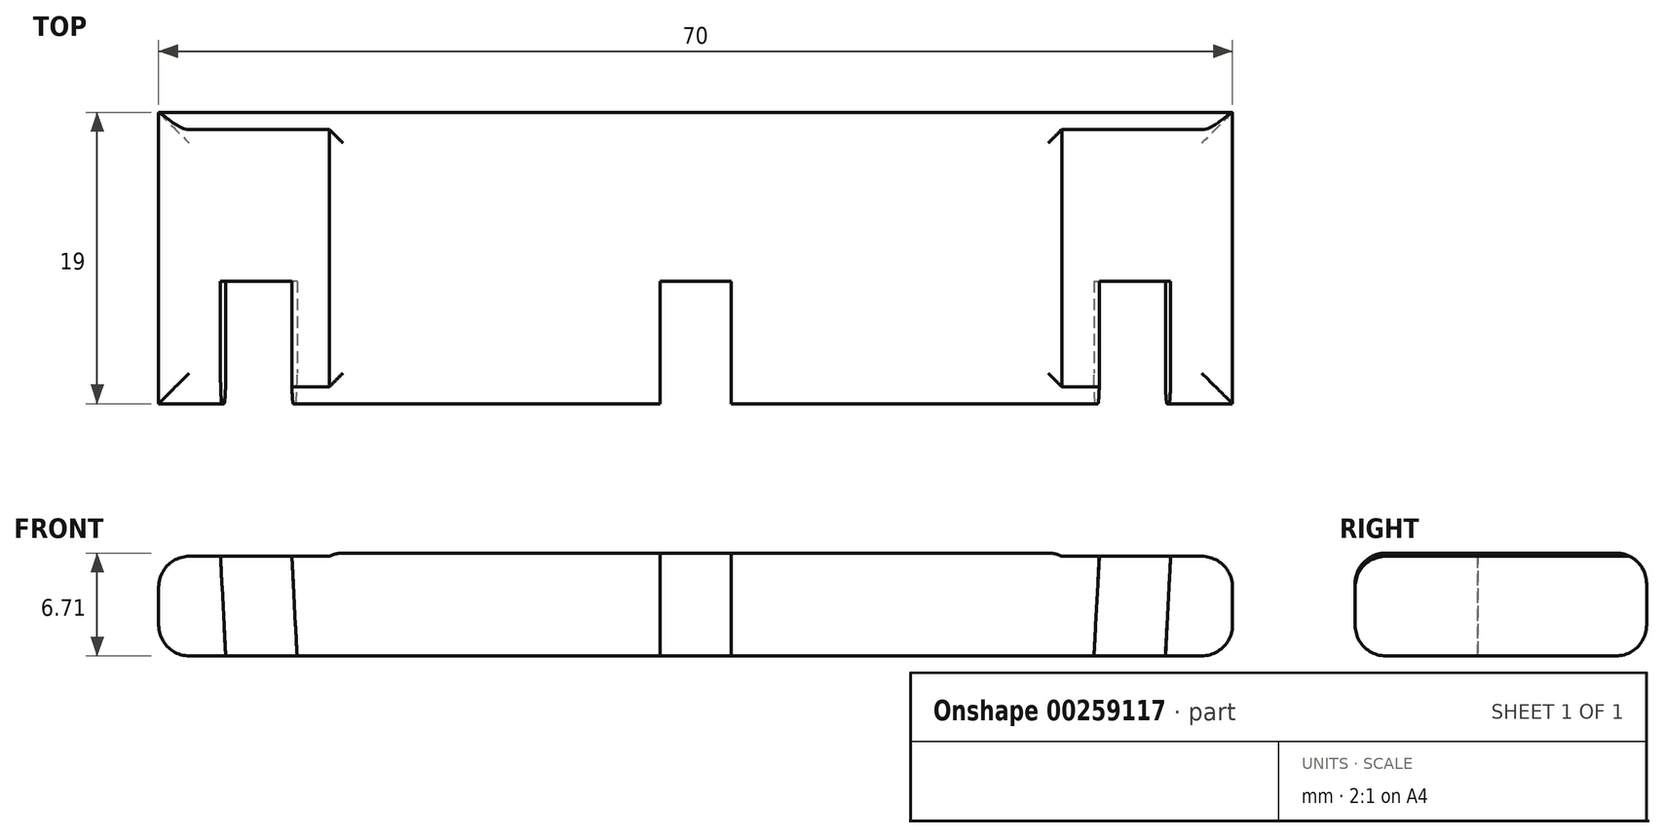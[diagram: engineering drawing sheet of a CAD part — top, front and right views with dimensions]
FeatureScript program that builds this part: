
annotation { "Feature Type Name" : "Feature", "Feature Type Description" : "" }
export const myFeature = defineFeature(function(context is Context, id is Id, definition is map)
    precondition{}
    {
        {
            var Q0;
            Q0=qCreatedBy(makeId("Top.planeOp"),FACE);
            var sketch = newSketch(context, id + "F0", { "sketchPlane" : qUnion([Q0])});
            skLineSegment(sketch, "E0.bottom", {"start": v(35, -9.5) * mm, "end": v(-35, -9.5) * mm});
            skLineSegment(sketch, "E0.top", {"start": v(35, 9.5) * mm, "end": v(-35, 9.5) * mm});
            skLineSegment(sketch, "E0.left", {"start": v(35, -9.5) * mm, "end": v(35, 9.5) * mm});
            skLineSegment(sketch, "E0.right", {"start": v(-35, -9.5) * mm, "end": v(-35, 9.5) * mm});
            skPoint(sketch, "E0.middle", {"position": v(0, 0) * mm});
            skLineSegment(sketch, "E1", {"start": v(0, 0) * mm, "end": v(0, -9.5) * mm, "construction": true});
            skLineSegment(sketch, "E2.bottom", {"start": v(2.33, -17.5) * mm, "end": v(-2.32, -17.5) * mm});
            skLineSegment(sketch, "E2.top", {"start": v(2.33, -1.5) * mm, "end": v(-2.33, -1.5) * mm});
            skLineSegment(sketch, "E2.left", {"start": v(2.33, -17.5) * mm, "end": v(2.33, -1.5) * mm});
            skLineSegment(sketch, "E2.right", {"start": v(-2.32, -17.5) * mm, "end": v(-2.32, -1.5) * mm});
            skPoint(sketch, "E2.middle", {"position": v(0, -9.5) * mm});
            skLineSegment(sketch, "E3.1.0.0", {"start": v(25.98, -17.5) * mm, "end": v(25.98, -1.5) * mm});
            skLineSegment(sketch, "E3.1.0.1", {"start": v(30.63, -1.5) * mm, "end": v(25.98, -1.5) * mm});
            skLineSegment(sketch, "E3.1.0.2", {"start": v(30.63, -17.5) * mm, "end": v(30.63, -1.5) * mm});
            skLineSegment(sketch, "E3.direction1", {"start": v(-2.32, -17.5) * mm, "end": v(25.98, -17.5) * mm, "construction": true});
            skLineSegment(sketch, "E4.1.0.0", {"start": v(-25.98, -1.5) * mm, "end": v(-30.63, -1.5) * mm});
            skLineSegment(sketch, "E4.1.0.1", {"start": v(-30.62, -17.5) * mm, "end": v(-30.62, -1.5) * mm});
            skLineSegment(sketch, "E4.1.0.2", {"start": v(-25.97, -17.5) * mm, "end": v(-25.97, -1.5) * mm});
            skLineSegment(sketch, "E4.direction1", {"start": v(-2.32, -17.5) * mm, "end": v(-30.62, -17.5) * mm, "construction": true});
            skLineSegment(sketch, "E5", {"start": v(-23.87, -9.5) * mm, "end": v(-23.87, 9.5) * mm});
            skLineSegment(sketch, "E6.MirrorCS", {"start": v(23.87, -9.5) * mm, "end": v(23.87, 9.5) * mm});
            skSolve(sketch);
        }
        {
            var Q0;
            {var subQ0=sQuery(id+"F0.wireOp",EDGE,"E2.top");Q0=makeQuery(id+"F0.imprint","IMPRINT",FACE,{"disambiguationData":[TD([[makeQuery(id+"F0.imprint","IMPRINT",EDGE,{"derivedFrom":subQ0}),-1.0]])]});}
            extrude(context, id + "F1", {"entities" : qUnion([Q0]), "depth" : 6.7 * mm});
        }
        {
            var Q0;
            {var subQ0=sQuery(id+"F0.wireOp",EDGE,"E0.right");Q0=makeQuery(id+"F0.imprint","IMPRINT",FACE,{"disambiguationData":[TD([[makeQuery(id+"F0.imprint","IMPRINT",EDGE,{"derivedFrom":subQ0}),-1.0]])]});}
            var Q1;
            {var subQ0=sQuery(id+"F0.wireOp",EDGE,"E0.left");Q1=makeQuery(id+"F0.imprint","IMPRINT",FACE,{"disambiguationData":[TD([[makeQuery(id+"F0.imprint","IMPRINT",EDGE,{"derivedFrom":subQ0}),1.0]])]});}
            var Q2;
            {var subQ5=sQuery(id+"F0.wireOp",EDGE,"E4.1.0.0");Q2=makeQuery(id+"F0.imprint","IMPRINT",FACE,{"disambiguationData":[TD([[makeQuery(id+"F0.imprint","IMPRINT",EDGE,{"derivedFrom":subQ5}),1.0]])]});}
            var Q3;
            {var subQ5=sQuery(id+"F0.wireOp",EDGE,"E3.1.0.1");Q3=makeQuery(id+"F0.imprint","IMPRINT",FACE,{"disambiguationData":[TD([[makeQuery(id+"F0.imprint","IMPRINT",EDGE,{"derivedFrom":subQ5}),1.0]])]});}
            extrude(context, id + "F2", {"entities" : qUnion([Q0, Q1, Q2, Q3]), "operationType" : NewBodyOperationType.ADD, "depth" : 6.5 * mm});
        }
        {
            var Q0;
            {var subQ0=sQuery(id+"F0.wireOp",EDGE,"E0.bottom");var subQ2=makeQuery(id+"F0.imprint","INTERSECT",VERTEX,{"derivedFrom":[subQ0,sQuery(id+"F0.wireOp",EDGE,"E4.1.0.2")]});var subQ3=makeQuery(id+"F0.imprint","INTERSECT",VERTEX,{"derivedFrom":[subQ0,sQuery(id+"F0.wireOp",EDGE,"E5")]});Q0=makeQuery(id+"F2.boolean.opBoolean","MERGE",FACE,{"derivedFrom":[makeQuery(id+"F1.opExtrude","SWEPT_FACE",FACE,{"disambiguationData":[OSD([subQ0]),TDD([makeQuery(id+"F0.imprint","IMPRINT",EDGE,{"disambiguationData":[TD([[subQ3,1.0]])],"derivedFrom":subQ0})])]}),makeQuery(id+"F2.opExtrude","SWEPT_FACE",FACE,{"disambiguationData":[OSD([subQ0]),TDD([makeQuery(id+"F0.imprint","IMPRINT",EDGE,{"disambiguationData":[TD([[subQ3,-1.0]])],"derivedFrom":subQ0}),makeQuery(id+"F0.imprint","IMPRINT",EDGE,{"disambiguationData":[TD([[subQ2,-1.0]])],"derivedFrom":subQ0}),makeQuery(id+"F0.imprint","IMPRINT",EDGE,{"disambiguationData":[TD([[makeQuery(id+"F0.imprint","INTERSECT",VERTEX,{"derivedFrom":[subQ0,sQuery(id+"F0.wireOp",EDGE,"E0.right")]}),1.0]])],"derivedFrom":subQ0})])]})]});}
            var sketch = newSketch(context, id + "F3", { "sketchPlane" : qUnion([Q0])});
            skLineSegment(sketch, "E7", {"start": v(-25.97, 6.7) * mm, "end": v(-25.97, 0) * mm, "construction": true});
            skLineSegment(sketch, "E8", {"start": v(-25.97, 0) * mm, "end": v(-26.32, 6.5) * mm});
            skLineSegment(sketch, "E9.0", {"start": v(-30.63, 0) * mm, "end": v(-30.97, 6.5) * mm});
            skLineSegment(sketch, "E10", {"start": v(25.97, 0) * mm, "end": v(25.97, 6.52) * mm, "construction": true});
            skLineSegment(sketch, "E11", {"start": v(25.97, 0) * mm, "end": v(26.34, 6.97) * mm});
            skLineSegment(sketch, "E12.0", {"start": v(30.62, -0.24) * mm, "end": v(30.98, 6.73) * mm});
            skLineSegment(sketch, "E13", {"start": v(26.34, 6.97) * mm, "end": v(30.98, 6.73) * mm});
            skLineSegment(sketch, "E14", {"start": v(30.62, -0.24) * mm, "end": v(25.97, 0) * mm});
            skSolve(sketch);
        }
        {
            var Q0;
            {var subQ0=sQuery(id+"F3.wireOp",EDGE,"E8");Q0=makeQuery(id+"F3.imprint","IMPRINT",FACE,{"disambiguationData":[TD([[makeQuery(id+"F3.imprint","IMPRINT",EDGE,{"derivedFrom":subQ0}),1.0]])]});}
            var Q1;
            Q1=makeQuery(id+"F3.imprint","IMPRINT",FACE,{"disambiguationData":[TD([[makeQuery(id+"F3.imprint","IMPRINT",EDGE,{"derivedFrom":sQuery(id+"F3.wireOp",EDGE,"E11")}),-1.0]])]});
            extrude(context, id + "F4", {"entities" : qUnion([Q0, Q1]), "operationType" : NewBodyOperationType.REMOVE, "oppositeDirection" : true, "depth" : 8 * mm});
        }
        {
            var Q0;
            Q0=makeQuery(id+"F1.opExtrude","CAP_EDGE",EDGE,{"disambiguationData":[OSD([sQuery(id+"F0.wireOp",EDGE,"E0.top")])],"isStart":false});
            var Q1;
            Q1=makeQuery(id+"F1.opExtrude","CAP_EDGE",EDGE,{"disambiguationData":[OSD([sQuery(id+"F0.wireOp",EDGE,"E0.right")])],"isStart":false});
            var Q2;
            {var subQ0=sQuery(id+"F0.wireOp",EDGE,"E0.bottom");Q2=makeQuery(id+"F1.opExtrude","CAP_EDGE",EDGE,{"disambiguationData":[OSD([subQ0]),TDD([makeQuery(id+"F0.imprint","IMPRINT",EDGE,{"disambiguationData":[TD([[makeQuery(id+"F0.imprint","INTERSECT",VERTEX,{"derivedFrom":[subQ0,sQuery(id+"F0.wireOp",EDGE,"E4.1.0.2")]}),1.0]])],"derivedFrom":subQ0})])],"isStart":false});}
            var Q3;
            {var subQ0=sQuery(id+"F0.wireOp",EDGE,"E0.bottom");Q3=makeQuery(id+"F1.opExtrude","CAP_EDGE",EDGE,{"disambiguationData":[OSD([subQ0]),TDD([makeQuery(id+"F0.imprint","IMPRINT",EDGE,{"disambiguationData":[TD([[makeQuery(id+"F0.imprint","INTERSECT",VERTEX,{"derivedFrom":[subQ0,sQuery(id+"F0.wireOp",EDGE,"E0.right")]}),1.0]])],"derivedFrom":subQ0})])],"isStart":false});}
            var Q4;
            {var subQ0=sQuery(id+"F0.wireOp",EDGE,"E0.bottom");Q4=makeQuery(id+"F1.opExtrude","CAP_EDGE",EDGE,{"disambiguationData":[OSD([subQ0]),TDD([makeQuery(id+"F0.imprint","IMPRINT",EDGE,{"disambiguationData":[TD([[makeQuery(id+"F0.imprint","INTERSECT",VERTEX,{"derivedFrom":[subQ0,sQuery(id+"F0.wireOp",EDGE,"E3.1.0.0")]}),-1.0]])],"derivedFrom":subQ0})])],"isStart":false});}
            var Q5;
            {var subQ0=sQuery(id+"F0.wireOp",EDGE,"E0.bottom");Q5=makeQuery(id+"F1.opExtrude","CAP_EDGE",EDGE,{"disambiguationData":[OSD([subQ0]),TDD([makeQuery(id+"F0.imprint","IMPRINT",EDGE,{"disambiguationData":[TD([[makeQuery(id+"F0.imprint","INTERSECT",VERTEX,{"derivedFrom":[subQ0,sQuery(id+"F0.wireOp",EDGE,"E0.left")]}),-1.0]])],"derivedFrom":subQ0})])],"isStart":false});}
            var Q6;
            {var subQ0=sQuery(id+"F0.wireOp",EDGE,"E0.bottom");Q6=makeQuery(id+"F1.opExtrude","CAP_EDGE",EDGE,{"disambiguationData":[OSD([subQ0]),TDD([makeQuery(id+"F0.imprint","IMPRINT",EDGE,{"disambiguationData":[TD([[makeQuery(id+"F0.imprint","INTERSECT",VERTEX,{"derivedFrom":[subQ0,sQuery(id+"F0.wireOp",EDGE,"E3.1.0.0")]}),-1.0]])],"derivedFrom":subQ0})])],"isStart":true});}
            var Q7;
            {var subQ0=sQuery(id+"F0.wireOp",EDGE,"E0.bottom");Q7=makeQuery(id+"F1.opExtrude","CAP_EDGE",EDGE,{"disambiguationData":[OSD([subQ0]),TDD([makeQuery(id+"F0.imprint","IMPRINT",EDGE,{"disambiguationData":[TD([[makeQuery(id+"F0.imprint","INTERSECT",VERTEX,{"derivedFrom":[subQ0,sQuery(id+"F0.wireOp",EDGE,"E4.1.0.2")]}),1.0]])],"derivedFrom":subQ0})])],"isStart":true});}
            var Q8;
            {var subQ0=sQuery(id+"F0.wireOp",EDGE,"E0.bottom");Q8=makeQuery(id+"F1.opExtrude","CAP_EDGE",EDGE,{"disambiguationData":[OSD([subQ0]),TDD([makeQuery(id+"F0.imprint","IMPRINT",EDGE,{"disambiguationData":[TD([[makeQuery(id+"F0.imprint","INTERSECT",VERTEX,{"derivedFrom":[subQ0,sQuery(id+"F0.wireOp",EDGE,"E0.right")]}),1.0]])],"derivedFrom":subQ0})])],"isStart":true});}
            var Q9;
            Q9=makeQuery(id+"F1.opExtrude","CAP_EDGE",EDGE,{"disambiguationData":[OSD([sQuery(id+"F0.wireOp",EDGE,"E0.right")])],"isStart":true});
            var Q10;
            Q10=makeQuery(id+"F1.opExtrude","CAP_EDGE",EDGE,{"disambiguationData":[OSD([sQuery(id+"F0.wireOp",EDGE,"E0.top")])],"isStart":true});
            var Q11;
            Q11=makeQuery(id+"F1.opExtrude","CAP_EDGE",EDGE,{"disambiguationData":[OSD([sQuery(id+"F0.wireOp",EDGE,"E0.left")])],"isStart":true});
            var Q12;
            {var subQ0=sQuery(id+"F0.wireOp",EDGE,"E0.bottom");Q12=makeQuery(id+"F1.opExtrude","CAP_EDGE",EDGE,{"disambiguationData":[OSD([subQ0]),TDD([makeQuery(id+"F0.imprint","IMPRINT",EDGE,{"disambiguationData":[TD([[makeQuery(id+"F0.imprint","INTERSECT",VERTEX,{"derivedFrom":[subQ0,sQuery(id+"F0.wireOp",EDGE,"E0.left")]}),-1.0]])],"derivedFrom":subQ0})])],"isStart":true});}
            var Q13;
            Q13=makeQuery(id+"F2.opExtrude","CAP_EDGE",EDGE,{"disambiguationData":[OSD([sQuery(id+"F0.wireOp",EDGE,"E0.right")])],"isStart":false});
            var Q14;
            Q14=makeQuery(id+"F2.opExtrude","CAP_EDGE",EDGE,{"disambiguationData":[OSD([sQuery(id+"F0.wireOp",EDGE,"E0.right")])],"isStart":true});
            var Q15;
            {var subQ0=sQuery(id+"F0.wireOp",EDGE,"E0.bottom");Q15=makeQuery(id+"F1.opExtrude","CAP_EDGE",EDGE,{"disambiguationData":[OSD([subQ0]),TDD([makeQuery(id+"F0.imprint","IMPRINT",EDGE,{"disambiguationData":[TD([[makeQuery(id+"F0.imprint","INTERSECT",VERTEX,{"derivedFrom":[subQ0,sQuery(id+"F0.wireOp",EDGE,"E5")]}),1.0]])],"derivedFrom":subQ0})])],"isStart":false});}
            var Q16;
            {var subQ2=sQuery(id+"F0.wireOp",EDGE,"E0.bottom");var subQ3=sQuery(id+"F0.wireOp",EDGE,"E5");var subQ4=makeQuery(id+"F0.imprint","INTERSECT",VERTEX,{"derivedFrom":[subQ2,subQ3]});var subQ5=sQuery(id+"F0.wireOp",EDGE,"E2.right");var subQ6=makeQuery(id+"F0.imprint","IMPRINT",EDGE,{"disambiguationData":[TD([[subQ4,1.0]])],"derivedFrom":subQ2});var subQ7=sQuery(id+"F0.wireOp",EDGE,"E0.right");var subQ9=makeQuery(id+"F0.imprint","IMPRINT",EDGE,{"disambiguationData":[TD([[makeQuery(id+"F0.imprint","INTERSECT",VERTEX,{"derivedFrom":[subQ2,subQ7]}),1.0]])],"derivedFrom":subQ2});var subQ10=makeQuery(id+"F0.imprint","INTERSECT",VERTEX,{"derivedFrom":[subQ2,sQuery(id+"F0.wireOp",EDGE,"E4.1.0.2")]});var subQ11=makeQuery(id+"F0.imprint","IMPRINT",EDGE,{"disambiguationData":[TD([[subQ10,-1.0]])],"derivedFrom":subQ2});var subQ12=makeQuery(id+"F0.imprint","IMPRINT",EDGE,{"disambiguationData":[TD([[subQ4,-1.0]])],"derivedFrom":subQ2});Q16=makeQuery(id+"F4.boolean.opBoolean","SPLIT",EDGE,{"disambiguationData":[TD([makeQuery(id+"F1.opExtrude","SWEPT_FACE",FACE,{"disambiguationData":[OSD([subQ5])]})])],"derivedFrom":makeQuery(id+"F2.boolean.opBoolean","MERGE",EDGE,{"derivedFrom":[makeQuery(id+"F1.opExtrude","CAP_EDGE",EDGE,{"disambiguationData":[OSD([subQ2]),TDD([subQ6])],"isStart":true}),makeQuery(id+"F2.opExtrude","CAP_EDGE",EDGE,{"disambiguationData":[OSD([subQ2]),TDD([subQ12,subQ11,subQ9])],"isStart":true})]})});}
            var Q17;
            {var subQ0=sQuery(id+"F0.wireOp",EDGE,"E0.bottom");Q17=makeQuery(id+"F1.opExtrude","CAP_EDGE",EDGE,{"disambiguationData":[OSD([subQ0]),TDD([makeQuery(id+"F0.imprint","IMPRINT",EDGE,{"disambiguationData":[TD([[makeQuery(id+"F0.imprint","INTERSECT",VERTEX,{"derivedFrom":[subQ0,sQuery(id+"F0.wireOp",EDGE,"E6.MirrorCS")]}),-1.0]])],"derivedFrom":subQ0})])],"isStart":false});}
            var Q18;
            {var subQ0=sQuery(id+"F0.wireOp",EDGE,"E6.MirrorCS");var subQ1=sQuery(id+"F0.wireOp",EDGE,"E0.bottom");var subQ2=makeQuery(id+"F0.imprint","INTERSECT",VERTEX,{"derivedFrom":[subQ1,subQ0]});var subQ4=makeQuery(id+"F0.imprint","IMPRINT",EDGE,{"disambiguationData":[TD([[subQ2,1.0]])],"derivedFrom":subQ1});var subQ5=makeQuery(id+"F0.imprint","INTERSECT",VERTEX,{"derivedFrom":[subQ1,sQuery(id+"F0.wireOp",EDGE,"E3.1.0.2")]});var subQ6=makeQuery(id+"F0.imprint","IMPRINT",EDGE,{"disambiguationData":[TD([[subQ5,-1.0]])],"derivedFrom":subQ1});var subQ7=sQuery(id+"F0.wireOp",EDGE,"E0.left");var subQ8=makeQuery(id+"F0.imprint","IMPRINT",EDGE,{"disambiguationData":[TD([[makeQuery(id+"F0.imprint","INTERSECT",VERTEX,{"derivedFrom":[subQ1,subQ7]}),-1.0]])],"derivedFrom":subQ1});var subQ9=sQuery(id+"F0.wireOp",EDGE,"E2.left");var subQ12=makeQuery(id+"F0.imprint","IMPRINT",EDGE,{"disambiguationData":[TD([[subQ2,-1.0]])],"derivedFrom":subQ1});Q18=makeQuery(id+"F4.boolean.opBoolean","SPLIT",EDGE,{"disambiguationData":[TD([makeQuery(id+"F1.opExtrude","SWEPT_FACE",FACE,{"disambiguationData":[OSD([subQ9])]})])],"derivedFrom":makeQuery(id+"F2.boolean.opBoolean","MERGE",EDGE,{"derivedFrom":[makeQuery(id+"F1.opExtrude","CAP_EDGE",EDGE,{"disambiguationData":[OSD([subQ1]),TDD([subQ12])],"isStart":true}),makeQuery(id+"F2.opExtrude","CAP_EDGE",EDGE,{"disambiguationData":[OSD([subQ1]),TDD([subQ8,subQ6,subQ4])],"isStart":true})]})});}
            var Q19;
            {var subQ0=sQuery(id+"F0.wireOp",EDGE,"E0.right");var subQ1=sQuery(id+"F0.wireOp",EDGE,"E5");var subQ2=sQuery(id+"F0.wireOp",EDGE,"E0.bottom");var subQ4=makeQuery(id+"F0.imprint","IMPRINT",EDGE,{"disambiguationData":[TD([[makeQuery(id+"F0.imprint","INTERSECT",VERTEX,{"derivedFrom":[subQ2,subQ0]}),1.0]])],"derivedFrom":subQ2});var subQ5=makeQuery(id+"F0.imprint","INTERSECT",VERTEX,{"derivedFrom":[subQ2,sQuery(id+"F0.wireOp",EDGE,"E4.1.0.2")]});var subQ6=makeQuery(id+"F0.imprint","IMPRINT",EDGE,{"disambiguationData":[TD([[subQ5,-1.0]])],"derivedFrom":subQ2});var subQ7=makeQuery(id+"F0.imprint","INTERSECT",VERTEX,{"derivedFrom":[subQ2,subQ1]});var subQ8=makeQuery(id+"F0.imprint","IMPRINT",EDGE,{"disambiguationData":[TD([[subQ7,-1.0]])],"derivedFrom":subQ2});Q19=makeQuery(id+"F4.boolean.opBoolean","SPLIT",EDGE,{"disambiguationData":[TD([makeQuery(id+"F2.opExtrude","SWEPT_FACE",FACE,{"disambiguationData":[OSD([subQ0])]})])],"derivedFrom":makeQuery(id+"F2.opExtrude","CAP_EDGE",EDGE,{"disambiguationData":[OSD([subQ2]),TDD([subQ8,subQ6,subQ4])],"isStart":false})});}
            var Q20;
            {var subQ0=sQuery(id+"F0.wireOp",EDGE,"E0.right");var subQ1=sQuery(id+"F0.wireOp",EDGE,"E0.bottom");var subQ3=makeQuery(id+"F0.imprint","IMPRINT",EDGE,{"disambiguationData":[TD([[makeQuery(id+"F0.imprint","INTERSECT",VERTEX,{"derivedFrom":[subQ1,subQ0]}),1.0]])],"derivedFrom":subQ1});var subQ4=makeQuery(id+"F0.imprint","INTERSECT",VERTEX,{"derivedFrom":[subQ1,sQuery(id+"F0.wireOp",EDGE,"E4.1.0.2")]});var subQ5=makeQuery(id+"F0.imprint","IMPRINT",EDGE,{"disambiguationData":[TD([[subQ4,-1.0]])],"derivedFrom":subQ1});var subQ6=sQuery(id+"F0.wireOp",EDGE,"E5");var subQ7=makeQuery(id+"F0.imprint","INTERSECT",VERTEX,{"derivedFrom":[subQ1,subQ6]});var subQ8=makeQuery(id+"F0.imprint","IMPRINT",EDGE,{"disambiguationData":[TD([[subQ7,-1.0]])],"derivedFrom":subQ1});var subQ12=makeQuery(id+"F0.imprint","IMPRINT",EDGE,{"disambiguationData":[TD([[subQ7,1.0]])],"derivedFrom":subQ1});Q20=makeQuery(id+"F4.boolean.opBoolean","SPLIT",EDGE,{"disambiguationData":[TD([makeQuery(id+"F2.opExtrude","SWEPT_FACE",FACE,{"disambiguationData":[OSD([subQ0])]})])],"derivedFrom":makeQuery(id+"F2.boolean.opBoolean","MERGE",EDGE,{"derivedFrom":[makeQuery(id+"F1.opExtrude","CAP_EDGE",EDGE,{"disambiguationData":[OSD([subQ1]),TDD([subQ12])],"isStart":true}),makeQuery(id+"F2.opExtrude","CAP_EDGE",EDGE,{"disambiguationData":[OSD([subQ1]),TDD([subQ8,subQ5,subQ3])],"isStart":true})]})});}
            var Q21;
            {var subQ0=sQuery(id+"F0.wireOp",EDGE,"E0.left");var subQ1=sQuery(id+"F0.wireOp",EDGE,"E6.MirrorCS");var subQ2=sQuery(id+"F0.wireOp",EDGE,"E0.bottom");var subQ3=makeQuery(id+"F0.imprint","INTERSECT",VERTEX,{"derivedFrom":[subQ2,subQ1]});var subQ5=makeQuery(id+"F0.imprint","IMPRINT",EDGE,{"disambiguationData":[TD([[subQ3,1.0]])],"derivedFrom":subQ2});var subQ6=makeQuery(id+"F0.imprint","INTERSECT",VERTEX,{"derivedFrom":[subQ2,sQuery(id+"F0.wireOp",EDGE,"E3.1.0.2")]});var subQ7=makeQuery(id+"F0.imprint","IMPRINT",EDGE,{"disambiguationData":[TD([[subQ6,-1.0]])],"derivedFrom":subQ2});var subQ8=makeQuery(id+"F0.imprint","IMPRINT",EDGE,{"disambiguationData":[TD([[makeQuery(id+"F0.imprint","INTERSECT",VERTEX,{"derivedFrom":[subQ2,subQ0]}),-1.0]])],"derivedFrom":subQ2});Q21=makeQuery(id+"F4.boolean.opBoolean","SPLIT",EDGE,{"disambiguationData":[TD([makeQuery(id+"F2.opExtrude","SWEPT_FACE",FACE,{"disambiguationData":[OSD([subQ0])]})])],"derivedFrom":makeQuery(id+"F2.opExtrude","CAP_EDGE",EDGE,{"disambiguationData":[OSD([subQ2]),TDD([subQ8,subQ7,subQ5])],"isStart":false})});}
            var Q22;
            {var subQ0=sQuery(id+"F0.wireOp",EDGE,"E6.MirrorCS");var subQ1=sQuery(id+"F0.wireOp",EDGE,"E0.left");var subQ3=sQuery(id+"F0.wireOp",EDGE,"E0.bottom");var subQ4=makeQuery(id+"F0.imprint","INTERSECT",VERTEX,{"derivedFrom":[subQ3,subQ0]});var subQ6=makeQuery(id+"F0.imprint","IMPRINT",EDGE,{"disambiguationData":[TD([[subQ4,1.0]])],"derivedFrom":subQ3});var subQ7=makeQuery(id+"F0.imprint","INTERSECT",VERTEX,{"derivedFrom":[subQ3,sQuery(id+"F0.wireOp",EDGE,"E3.1.0.2")]});var subQ8=makeQuery(id+"F0.imprint","IMPRINT",EDGE,{"disambiguationData":[TD([[subQ7,-1.0]])],"derivedFrom":subQ3});var subQ9=makeQuery(id+"F0.imprint","IMPRINT",EDGE,{"disambiguationData":[TD([[makeQuery(id+"F0.imprint","INTERSECT",VERTEX,{"derivedFrom":[subQ3,subQ1]}),-1.0]])],"derivedFrom":subQ3});var subQ12=makeQuery(id+"F0.imprint","IMPRINT",EDGE,{"disambiguationData":[TD([[subQ4,-1.0]])],"derivedFrom":subQ3});Q22=makeQuery(id+"F4.boolean.opBoolean","SPLIT",EDGE,{"disambiguationData":[TD([makeQuery(id+"F2.opExtrude","SWEPT_FACE",FACE,{"disambiguationData":[OSD([subQ1])]})])],"derivedFrom":makeQuery(id+"F2.boolean.opBoolean","MERGE",EDGE,{"derivedFrom":[makeQuery(id+"F1.opExtrude","CAP_EDGE",EDGE,{"disambiguationData":[OSD([subQ3]),TDD([subQ12])],"isStart":true}),makeQuery(id+"F2.opExtrude","CAP_EDGE",EDGE,{"disambiguationData":[OSD([subQ3]),TDD([subQ9,subQ8,subQ6])],"isStart":true})]})});}
            var Q23;
            Q23=makeQuery(id+"F2.opExtrude","CAP_EDGE",EDGE,{"disambiguationData":[OSD([sQuery(id+"F0.wireOp",EDGE,"E0.left")])],"isStart":true});
            var Q24;
            Q24=makeQuery(id+"F2.opExtrude","CAP_EDGE",EDGE,{"disambiguationData":[OSD([sQuery(id+"F0.wireOp",EDGE,"E0.left")])],"isStart":false});
            var Q25;
            Q25=makeQuery(id+"F1.opExtrude","CAP_EDGE",EDGE,{"disambiguationData":[OSD([sQuery(id+"F0.wireOp",EDGE,"E6.MirrorCS")])],"isStart":false});
            var Q26;
            Q26=makeQuery(id+"F1.opExtrude","CAP_EDGE",EDGE,{"disambiguationData":[OSD([sQuery(id+"F0.wireOp",EDGE,"E5")])],"isStart":false});
            fillet(context, id + "F5", {"entities" : qUnion([Q0, Q1, Q2, Q3, Q4, Q5, Q6, Q7, Q8, Q9, Q10, Q11, Q12, Q13, Q14, Q15, Q16, Q17, Q18, Q19, Q20, Q21, Q22, Q23, Q24, Q25, Q26]), "radius" : 2 * mm, "tangentPropagation" : true, "allowEdgeOverflow" : false});
        }
    });
